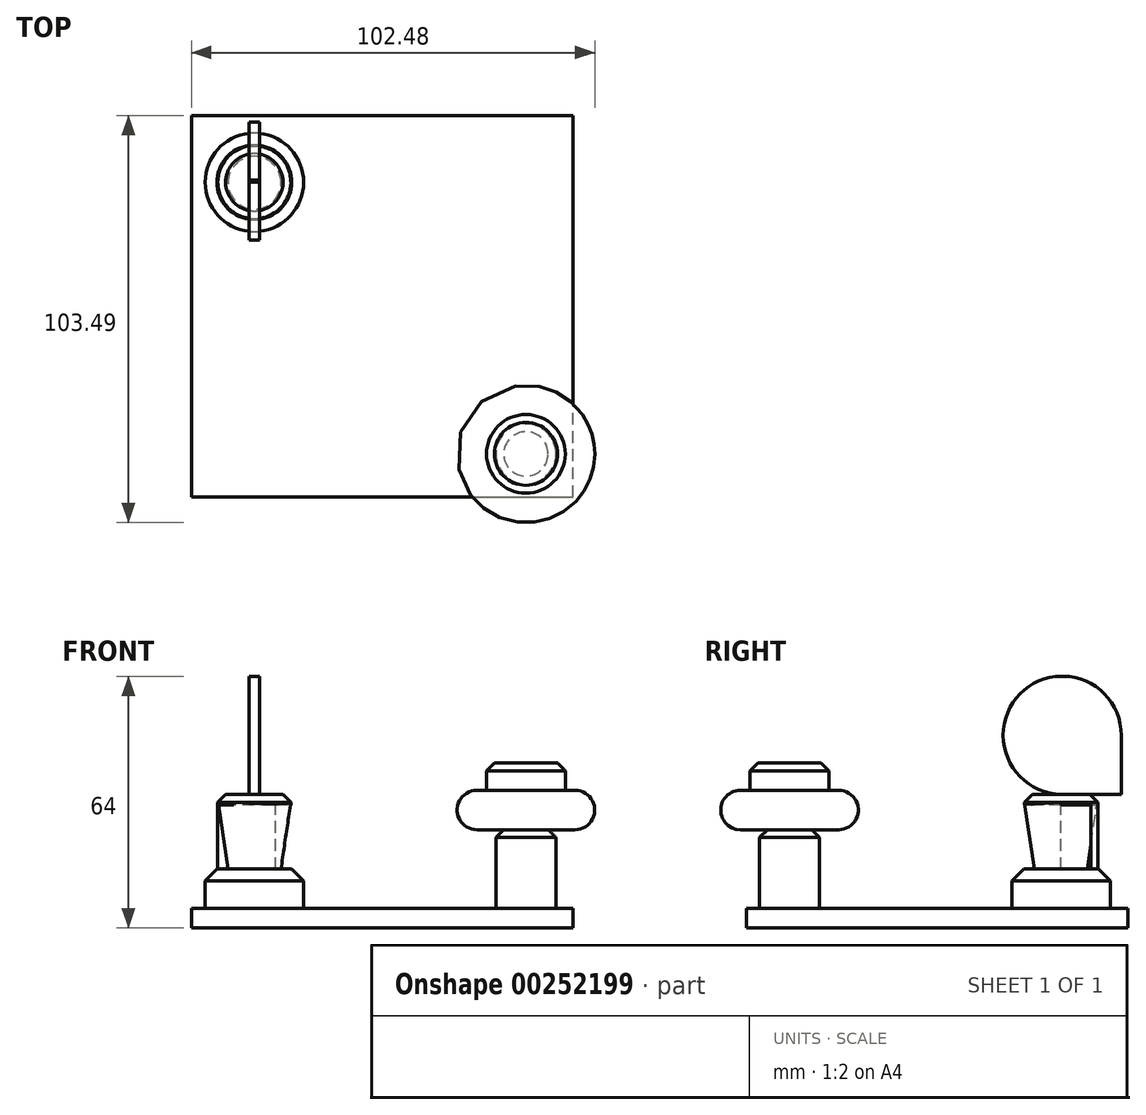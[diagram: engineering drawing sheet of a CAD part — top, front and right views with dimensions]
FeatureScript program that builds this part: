
annotation { "Feature Type Name" : "Feature", "Feature Type Description" : "" }
export const myFeature = defineFeature(function(context is Context, id is Id, definition is map)
    precondition{}
    {
        {
            var Q0;
            Q0=qCreatedBy(makeId("Front.planeOp"),FACE);
            var sketch = newSketch(context, id + "F0", { "sketchPlane" : qUnion([Q0])});
            skLineSegment(sketch, "E0.bottom", {"start": v(-47.2, 2.25) * mm, "end": v(49.8, 2.25) * mm});
            skLineSegment(sketch, "E0.top", {"start": v(-47.2, -2.75) * mm, "end": v(49.8, -2.75) * mm});
            skLineSegment(sketch, "E0.left", {"start": v(-47.2, 2.25) * mm, "end": v(-47.2, -2.75) * mm});
            skLineSegment(sketch, "E0.right", {"start": v(49.8, 2.25) * mm, "end": v(49.8, -2.75) * mm});
            skSolve(sketch);
        }
        {
            var Q0;
            Q0 = qSketchRegion(id + "F0", true);
            extrude(context, id + "F1", {"entities" : qUnion([Q0]), "endBound" : BoundingType.SYMMETRIC, "depth" : 97 * mm});
        }
        {
            var Q0;
            Q0=makeQuery(id+"F1.opExtrude","SWEPT_FACE",FACE,{"disambiguationData":[OSD([sQuery(id+"F0.wireOp",EDGE,"E0.bottom")])]});
            var sketch = newSketch(context, id + "F2", { "sketchPlane" : qUnion([Q0])});
            skLineSegment(sketch, "E1", {"start": v(37.8, -48.5) * mm, "end": v(37.8, -37.5) * mm, "construction": true});
            skLineSegment(sketch, "E2", {"start": v(37.8, -37.5) * mm, "end": v(49.8, -37.5) * mm, "construction": true});
            skCircle(sketch, "E3", {"center": v(37.8, -37.5) * mm, "radius": 7.65 * mm});
            skSolve(sketch);
        }
        {
            var Q0;
            Q0 = qSketchRegion(id + "F2", true);
            extrude(context, id + "F3", {"entities" : qUnion([Q0]), "operationType" : NewBodyOperationType.ADD, "depth" : 20 * mm});
        }
        {
            var Q0;
            Q0=makeQuery(id+"F3.opExtrude","CAP_EDGE",EDGE,{"disambiguationData":[OSD([sQuery(id+"F2.wireOp",EDGE,"E3")])],"isStart":false});
            chamfer(context, id + "F4", {"entities" : qUnion([Q0]), "width" : 2 * mm, "tangentPropagation" : true});
        }
        {
            var Q0;
            Q0=makeQuery(id+"F3.opExtrude","CAP_FACE",FACE,{"disambiguationData":[OSD([sQuery(id+"F2.wireOp",EDGE,"E3")])],"isStart":false});
            var sketch = newSketch(context, id + "F5", { "sketchPlane" : qUnion([Q0])});
            skCircle(sketch, "E4", {"center": v(37.8, -37.5) * mm, "radius": 17.49 * mm});
            skSolve(sketch);
        }
        {
            var Q0;
            Q0 = qSketchRegion(id + "F5", true);
            extrude(context, id + "F6", {"entities" : qUnion([Q0]), "operationType" : NewBodyOperationType.ADD, "depth" : 10 * mm});
        }
        {
            var Q0;
            Q0=makeQuery(id+"F6.opExtrude","SWEPT_FACE",FACE,{"disambiguationData":[OSD([sQuery(id+"F5.wireOp",EDGE,"E4")])]});
            fillet(context, id + "F7", {"entities" : qUnion([Q0]), "radius" : 5 * mm, "tangentPropagation" : true, "allowEdgeOverflow" : false});
        }
        {
            var Q0;
            Q0=makeQuery(id+"F6.opExtrude","CAP_FACE",FACE,{"disambiguationData":[OSD([sQuery(id+"F5.wireOp",EDGE,"E4")])],"isStart":false});
            var sketch = newSketch(context, id + "F8", { "sketchPlane" : qUnion([Q0])});
            skCircle(sketch, "E5", {"center": v(37.8, -37.5) * mm, "radius": 10 * mm});
            skSolve(sketch);
        }
        {
            var Q0;
            Q0 = qSketchRegion(id + "F8", true);
            extrude(context, id + "F9", {"entities" : qUnion([Q0]), "operationType" : NewBodyOperationType.ADD, "depth" : 7 * mm});
        }
        {
            var Q0;
            Q0=makeQuery(id+"F9.opExtrude","CAP_EDGE",EDGE,{"disambiguationData":[OSD([sQuery(id+"F8.wireOp",EDGE,"E5")])],"isStart":false});
            chamfer(context, id + "F10", {"entities" : qUnion([Q0]), "width" : 2 * mm, "tangentPropagation" : true});
        }
        {
            var Q0;
            Q0=makeQuery(id+"F1.opExtrude","SWEPT_FACE",FACE,{"disambiguationData":[OSD([sQuery(id+"F0.wireOp",EDGE,"E0.bottom")])]});
            var sketch = newSketch(context, id + "F11", { "sketchPlane" : qUnion([Q0])});
            skLineSegment(sketch, "E6", {"start": v(-31.2, 48.5) * mm, "end": v(-31.2, 31.5) * mm, "construction": true});
            skLineSegment(sketch, "E7", {"start": v(-31.2, 31.5) * mm, "end": v(-47.2, 31.5) * mm, "construction": true});
            skCircle(sketch, "E8", {"center": v(-31.2, 31.5) * mm, "radius": 12.5 * mm});
            skSolve(sketch);
        }
        {
            var Q0;
            Q0 = qSketchRegion(id + "F11", true);
            extrude(context, id + "F12", {"entities" : qUnion([Q0]), "operationType" : NewBodyOperationType.ADD, "depth" : 10 * mm});
        }
        {
            var Q0;
            Q0=makeQuery(id+"F12.opExtrude","CAP_EDGE",EDGE,{"disambiguationData":[OSD([sQuery(id+"F11.wireOp",EDGE,"E8")])],"isStart":false});
            chamfer(context, id + "F13", {"entities" : qUnion([Q0]), "width" : 3 * mm, "tangentPropagation" : true});
        }
        {
            var Q0;
            Q0=makeQuery(id+"F12.opExtrude","CAP_FACE",FACE,{"disambiguationData":[OSD([sQuery(id+"F11.wireOp",EDGE,"E8")])],"isStart":false});
            var sketch = newSketch(context, id + "F14", { "sketchPlane" : qUnion([Q0])});
            skCircle(sketch, "E9", {"center": v(-31.2, 31.5) * mm, "radius": 9.28 * mm});
            skSolve(sketch);
        }
        {
            var Q0;
            Q0 = qSketchRegion(id + "F14", true);
            extrude(context, id + "F15", {"entities" : qUnion([Q0]), "operationType" : NewBodyOperationType.ADD, "depth" : 19 * mm});
        }
        {
            var Q0;
            Q0=makeQuery(id+"F15.opExtrude","CAP_EDGE",EDGE,{"disambiguationData":[OSD([sQuery(id+"F14.wireOp",EDGE,"E9")])],"isStart":false});
            chamfer(context, id + "F16", {"entities" : qUnion([Q0]), "width" : 2 * mm, "tangentPropagation" : true});
        }
        {
            var Q0;
            Q0=makeQuery(id+"F15.opExtrude","CAP_FACE",FACE,{"disambiguationData":[OSD([sQuery(id+"F14.wireOp",EDGE,"E9")])],"isStart":false});
            var sketch = newSketch(context, id + "F17", { "sketchPlane" : qUnion([Q0])});
            skLineSegment(sketch, "E10.bottom", {"start": v(-29.85, 46.78) * mm, "end": v(-32.56, 46.78) * mm});
            skLineSegment(sketch, "E10.top", {"start": v(-29.85, 16.22) * mm, "end": v(-32.56, 16.22) * mm});
            skLineSegment(sketch, "E10.left", {"start": v(-29.85, 46.78) * mm, "end": v(-29.85, 16.22) * mm});
            skLineSegment(sketch, "E10.right", {"start": v(-32.56, 46.78) * mm, "end": v(-32.56, 16.22) * mm});
            skPoint(sketch, "E10.middle", {"position": v(-31.2, 31.5) * mm});
            skSolve(sketch);
        }
        {
            var Q0;
            Q0 = qSketchRegion(id + "F17", true);
            extrude(context, id + "F18", {"entities" : qUnion([Q0]), "operationType" : NewBodyOperationType.ADD, "depth" : 30 * mm});
        }
        {
            var Q0;
            Q0=makeQuery(id+"F18.opExtrude","SWEPT_FACE",FACE,{"disambiguationData":[OSD([sQuery(id+"F17.wireOp",EDGE,"E10.left")])]});
            var sketch = newSketch(context, id + "F19", { "sketchPlane" : qUnion([Q0])});
            skLineSegment(sketch, "E11", {"start": v(31.5, 61.25) * mm, "end": v(31.5, 31.25) * mm, "construction": true});
            skLineSegment(sketch, "E12", {"start": v(46.78, 46.25) * mm, "end": v(16.22, 46.25) * mm, "construction": true});
            skArc(sketch, "E13", {"start": v(31.5, 61.25) * mm, "mid": v(21.26, 35.55) * mm, "end": v(46.78, 46.25) * mm});
            skCircle(sketch, "E14", {"center": v(31.77, 46.25) * mm, "radius": 15 * mm});
            skSolve(sketch);
        }
        {
            var Q0;
            {var subQ0=sQuery(id+"F19.wireOp",EDGE,"E14");var subQ1=sQuery(id+"F17.wireOp",EDGE,"E10.left");var subQ2=makeQuery(id+"F18.opExtrude","CAP_EDGE",EDGE,{"disambiguationData":[OSD([subQ1])],"isStart":false});var subQ3=makeQuery(id+"F19.imprint","INTERSECT",VERTEX,{"disambiguationData":[OD(1.0)],"derivedFrom":[subQ2,subQ0]});Q0=makeQuery(id+"F19.imprint","IMPRINT",FACE,{"disambiguationData":[TD([[makeQuery(id+"F19.imprint","IMPRINT",EDGE,{"disambiguationData":[TD([[subQ3,1.0]])],"derivedFrom":subQ0}),-1.0]])]});}
            var Q1;
            {var subQ0=sQuery(id+"F17.wireOp",EDGE,"E10.left");var subQ2=sQuery(id+"F17.wireOp",EDGE,"E10.top");var subQ3=makeQuery(id+"F18.opExtrude","SWEPT_EDGE",EDGE,{"disambiguationData":[OSD([subQ2,subQ0])]});Q1=makeQuery(id+"F19.imprint","IMPRINT",FACE,{"disambiguationData":[TD([[makeQuery(id+"F19.imprint","IMPRINT",EDGE,{"derivedFrom":subQ3}),1.0]])]});}
            var Q2;
            {var subQ0=sQuery(id+"F19.wireOp",EDGE,"E14");var subQ1=sQuery(id+"F17.wireOp",EDGE,"E10.left");var subQ2=sQuery(id+"F17.wireOp",EDGE,"E10.bottom");var subQ3=makeQuery(id+"F18.opExtrude","SWEPT_EDGE",EDGE,{"disambiguationData":[OSD([subQ2,subQ1])]});var subQ4=makeQuery(id+"F19.imprint","INTERSECT",VERTEX,{"derivedFrom":[subQ3,subQ0]});Q2=makeQuery(id+"F19.imprint","IMPRINT",FACE,{"disambiguationData":[TD([[makeQuery(id+"F19.imprint","IMPRINT",EDGE,{"disambiguationData":[TD([[subQ4,1.0]])],"derivedFrom":subQ0}),-1.0]])]});}
            extrude(context, id + "F20", {"entities" : qUnion([Q0, Q1, Q2]), "operationType" : NewBodyOperationType.REMOVE, "endBound" : BoundingType.THROUGH_ALL, "oppositeDirection" : true, "depth" : 60 * mm});
        }
        {
            var Q0;
            Q0=qCreatedBy(makeId("Front.planeOp"),FACE);
            cPlane(context, id + "F21", {"entities" : qUnion([Q0]), "cplaneType" : CPlaneType.OFFSET, "offset" : 31.4 * mm, "oppositeDirection" : true, "width" : 150 * mm, "height" : 150 * mm});
        }
        {
            var Q0;
            Q0=qCreatedBy(id+"F21.planeOp",FACE);
            var sketch = newSketch(context, id + "F22", { "sketchPlane" : qUnion([Q0])});
            skLineSegment(sketch, "E15", {"start": v(-21.93, 29.25) * mm, "end": v(-24.44, 12.25) * mm});
            skLineSegment(sketch, "E16", {"start": v(-24.44, 12.25) * mm, "end": v(-21.93, 12.25) * mm});
            skLineSegment(sketch, "E17", {"start": v(-21.93, 29.25) * mm, "end": v(-21.93, 12.25) * mm});
            skLineSegment(sketch, "E18", {"start": v(-40.48, 29.25) * mm, "end": v(-40.48, 12.25) * mm});
            skLineSegment(sketch, "E19", {"start": v(-40.48, 29.25) * mm, "end": v(-37.92, 12.25) * mm});
            skLineSegment(sketch, "E20", {"start": v(-37.92, 12.25) * mm, "end": v(-40.48, 12.25) * mm});
            skLineSegment(sketch, "E21", {"start": v(-21.93, 12.25) * mm, "end": v(-24.44, 12.25) * mm});
            skLineSegment(sketch, "E22", {"start": v(-24.44, 12.25) * mm, "end": v(-21.93, 29.25) * mm});
            skLineSegment(sketch, "E23", {"start": v(-31.15, 12.25) * mm, "end": v(-31.15, 29.02) * mm, "construction": true});
            skSolve(sketch);
        }
        {
            var Q0;
            Q0 = qSketchRegion(id + "F22", true);
            var Q1;
            Q1=sQuery(id+"F22.wireOp",EDGE,"E22");
            var Q2;
            Q2=sQuery(id+"F22.wireOp",EDGE,"E21");
            var Q3;
            Q3=sQuery(id+"F22.wireOp",EDGE,"E17");
            var Q4;
            Q4=sQuery(id+"F22.wireOp",EDGE,"E23");
            revolve(context, id + "F23", {"operationType" : NewBodyOperationType.REMOVE, "entities" : qUnion([Q0]), "surfaceEntities" : qUnion([Q1, Q2, Q3]), "axis" : qUnion([Q4]), "revolveType" : RevolveType.FULL, "oppositeDirection" : true});
        }
    });
